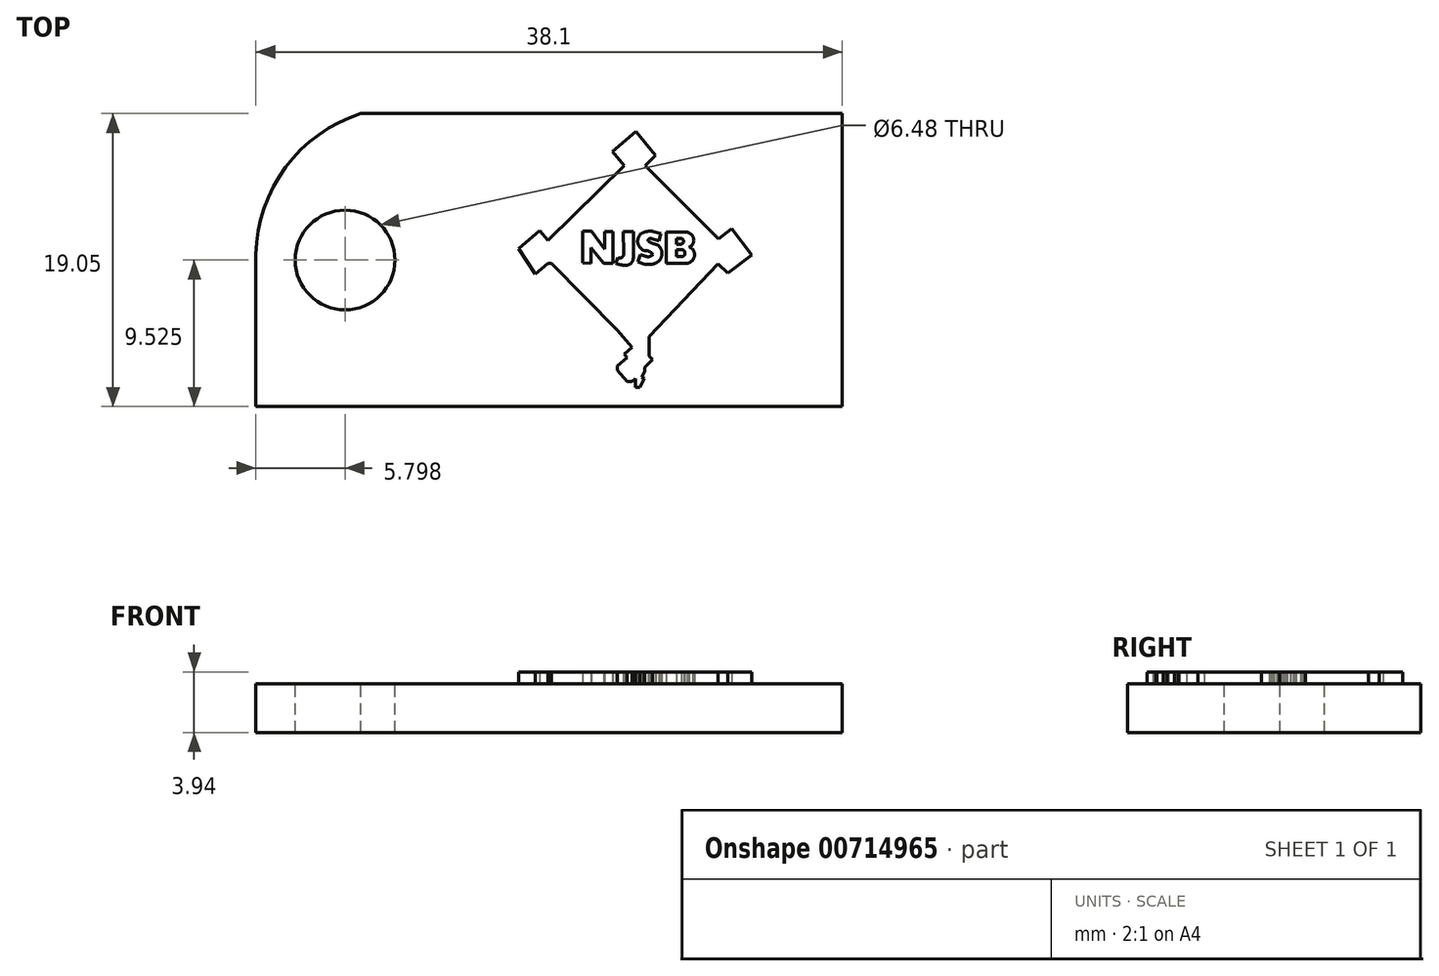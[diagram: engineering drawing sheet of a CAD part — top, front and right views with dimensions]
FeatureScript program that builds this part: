
annotation { "Feature Type Name" : "Feature", "Feature Type Description" : "" }
export const myFeature = defineFeature(function(context is Context, id is Id, definition is map)
    precondition{}
    {
        {
            var Q0;
            Q0=qCreatedBy(makeId("Top.planeOp"),FACE);
            var sketch = newSketch(context, id + "F0", { "sketchPlane" : qUnion([Q0])});
            skLineSegment(sketch, "E0.bottom", {"start": v(0, 0) * mm, "end": v(-38.1, 0) * mm});
            skLineSegment(sketch, "E0.top", {"start": v(0, 19.05) * mm, "end": v(-38.1, 19.05) * mm});
            skLineSegment(sketch, "E0.left", {"start": v(0, 0) * mm, "end": v(0, 19.05) * mm});
            skLineSegment(sketch, "E0.right", {"start": v(-38.1, 0) * mm, "end": v(-38.1, 19.05) * mm});
            skSolve(sketch);
        }
        {
            var Q0;
            Q0=qSketchRegion(id+"F0",true);
            extrude(context, id + "F1", {"entities" : qUnion([Q0]), "depth" : 3.17 * mm, "offsetDistance" : 25.4 * mm});
        }
        {
            var Q0;
            Q0=makeQuery(id+"F1.opExtrude","CAP_FACE",FACE,{"disambiguationData":[OSD([sQuery(id+"F0.wireOp",EDGE,"E0.bottom"),sQuery(id+"F0.wireOp",EDGE,"E0.top"),sQuery(id+"F0.wireOp",EDGE,"E0.left"),sQuery(id+"F0.wireOp",EDGE,"E0.right")])],"isStart":false});
            var sketch = newSketch(context, id + "F2", { "sketchPlane" : qUnion([Q0])});
            skLineSegment(sketch, "E1", {"start": v(-38.1, 9.52) * mm, "end": v(0, 9.52) * mm, "construction": true});
            skArc(sketch, "E2", {"start": v(-31.28, 19.05) * mm, "mid": v(-36.27, 15.42) * mm, "end": v(-38.1, 9.52) * mm});
            skArc(sketch, "E3.MirrorCS", {"start": v(-31.28, 0) * mm, "mid": v(-36.27, 3.63) * mm, "end": v(-38.1, 9.52) * mm});
            skCircle(sketch, "E4", {"center": v(-32.3, 9.52) * mm, "radius": 3.24 * mm});
            skSolve(sketch);
        }
        {
            var Q0;
            {var subQ0=sQuery(id+"F2.wireOp",EDGE,"E2");var subQ1=makeQuery(id+"F1.opExtrude","CAP_EDGE",EDGE,{"disambiguationData":[OSD([sQuery(id+"F0.wireOp",EDGE,"E0.top")])],"isStart":false});var subQ2=makeQuery(id+"F2.imprint","INTERSECT",VERTEX,{"derivedFrom":[subQ1,subQ0]});Q0=makeQuery(id+"F2.imprint","IMPRINT",FACE,{"disambiguationData":[TD([[makeQuery(id+"F2.imprint","IMPRINT",EDGE,{"disambiguationData":[TD([[subQ2,-1.0]])],"derivedFrom":subQ0}),-1.0]])]});}
            var Q1;
            {var subQ0=sQuery(id+"F2.wireOp",EDGE,"E3.MirrorCS");var subQ1=makeQuery(id+"F1.opExtrude","CAP_EDGE",EDGE,{"disambiguationData":[OSD([sQuery(id+"F0.wireOp",EDGE,"E0.bottom")])],"isStart":false});var subQ2=makeQuery(id+"F2.imprint","INTERSECT",VERTEX,{"derivedFrom":[subQ1,subQ0]});Q1=makeQuery(id+"F2.imprint","IMPRINT",FACE,{"disambiguationData":[TD([[makeQuery(id+"F2.imprint","IMPRINT",EDGE,{"disambiguationData":[TD([[subQ2,-1.0]])],"derivedFrom":subQ0}),1.0]])]});}
            var Q2;
            Q2=makeQuery(id+"F2.imprint","IMPRINT",FACE,{"disambiguationData":[TD([[makeQuery(id+"F2.imprint","IMPRINT",EDGE,{"derivedFrom":sQuery(id+"F2.wireOp",EDGE,"E4")}),1.0]])]});
            extrude(context, id + "F3", {"entities" : qUnion([Q0, Q1, Q2]), "operationType" : NewBodyOperationType.REMOVE, "endBound" : BoundingType.THROUGH_ALL, "oppositeDirection" : true, "depth" : 25.4 * mm, "offsetDistance" : 25.4 * mm});
        }
        {
            var Q0;
            Q0=makeQuery(id+"F1.opExtrude","CAP_FACE",FACE,{"disambiguationData":[OSD([sQuery(id+"F0.wireOp",EDGE,"E0.bottom"),sQuery(id+"F0.wireOp",EDGE,"E0.top"),sQuery(id+"F0.wireOp",EDGE,"E0.left"),sQuery(id+"F0.wireOp",EDGE,"E0.right")])],"isStart":false});
            var sketch = newSketch(context, id + "F4", { "sketchPlane" : qUnion([Q0])});
            skLineSegment(sketch, "E5", {"start": v(-13.42, 17.87) * mm, "end": v(-14.93, 16.58) * mm});
            skLineSegment(sketch, "E6", {"start": v(-14.93, 16.58) * mm, "end": v(-14.16, 15.67) * mm});
            skLineSegment(sketch, "E7", {"start": v(-14.16, 15.67) * mm, "end": v(-19.11, 10.8) * mm});
            skLineSegment(sketch, "E8", {"start": v(-19.11, 10.8) * mm, "end": v(-19.65, 11.43) * mm});
            skLineSegment(sketch, "E9", {"start": v(-19.65, 11.43) * mm, "end": v(-21.03, 10.26) * mm});
            skLineSegment(sketch, "E10", {"start": v(-21.03, 10.26) * mm, "end": v(-19.95, 8.6) * mm});
            skLineSegment(sketch, "E11", {"start": v(-19.95, 8.6) * mm, "end": v(-19.11, 9.32) * mm});
            skLineSegment(sketch, "E12", {"start": v(-18.89, 9.32) * mm, "end": v(-14.6, 4.97) * mm});
            skLineSegment(sketch, "E13", {"start": v(-14.6, 4.97) * mm, "end": v(-14.42, 4.75) * mm});
            skLineSegment(sketch, "E14", {"start": v(-14.42, 4.75) * mm, "end": v(-14.17, 4.46) * mm});
            skLineSegment(sketch, "E15", {"start": v(-14.17, 4.46) * mm, "end": v(-13.64, 3.84) * mm});
            skLineSegment(sketch, "E16", {"start": v(-13.64, 3.84) * mm, "end": v(-14.17, 3.4) * mm});
            skLineSegment(sketch, "E17", {"start": v(-14.17, 3.4) * mm, "end": v(-13.99, 3.18) * mm});
            skLineSegment(sketch, "E18", {"start": v(-13.99, 3.18) * mm, "end": v(-14.6, 2.65) * mm});
            skLineSegment(sketch, "E19", {"start": v(-14.6, 2.65) * mm, "end": v(-14.6, 2.37) * mm});
            skLineSegment(sketch, "E20", {"start": v(-14.6, 2.37) * mm, "end": v(-14.35, 2.06) * mm});
            skLineSegment(sketch, "E21", {"start": v(-14.35, 2.06) * mm, "end": v(-13.99, 1.64) * mm});
            skLineSegment(sketch, "E22", {"start": v(-13.99, 1.64) * mm, "end": v(-13.64, 1.64) * mm});
            skLineSegment(sketch, "E23", {"start": v(-13.64, 1.64) * mm, "end": v(-13.43, 1.82) * mm});
            skLineSegment(sketch, "E24", {"start": v(-13.43, 1.82) * mm, "end": v(-13.43, 1.24) * mm});
            skLineSegment(sketch, "E25", {"start": v(-13.43, 1.24) * mm, "end": v(-13.16, 1.24) * mm});
            skLineSegment(sketch, "E26", {"start": v(-13.16, 1.24) * mm, "end": v(-12.87, 1.82) * mm});
            skLineSegment(sketch, "E27", {"start": v(-12.87, 1.82) * mm, "end": v(-13.03, 1.9) * mm});
            skLineSegment(sketch, "E28", {"start": v(-13.03, 1.9) * mm, "end": v(-12.83, 2.3) * mm});
            skLineSegment(sketch, "E29", {"start": v(-12.83, 2.3) * mm, "end": v(-12.83, 2.56) * mm});
            skLineSegment(sketch, "E30", {"start": v(-12.83, 2.56) * mm, "end": v(-12.33, 3.04) * mm});
            skLineSegment(sketch, "E31", {"start": v(-12.33, 3.04) * mm, "end": v(-12.55, 3.28) * mm});
            skLineSegment(sketch, "E32", {"start": v(-12.55, 3.28) * mm, "end": v(-12.55, 3.91) * mm});
            skLineSegment(sketch, "E33", {"start": v(-12.55, 3.91) * mm, "end": v(-12.55, 4.56) * mm});
            skLineSegment(sketch, "E34", {"start": v(-12.55, 4.56) * mm, "end": v(-12.94, 4.56) * mm});
            skLineSegment(sketch, "E35", {"start": v(-12.94, 4.56) * mm, "end": v(-12.94, 5.1) * mm});
            skLineSegment(sketch, "E36", {"start": v(-12.94, 5.1) * mm, "end": v(-12.68, 5.36) * mm});
            skLineSegment(sketch, "E37", {"start": v(-12.68, 5.36) * mm, "end": v(-12.68, 6.07) * mm});
            skLineSegment(sketch, "E38", {"start": v(-12.68, 6.07) * mm, "end": v(-14.16, 6.48) * mm});
            skLineSegment(sketch, "E39", {"start": v(-14.16, 6.48) * mm, "end": v(-14.24, 6.2) * mm});
            skLineSegment(sketch, "E40", {"start": v(-14.24, 6.2) * mm, "end": v(-14.51, 5.62) * mm});
            skLineSegment(sketch, "E41", {"start": v(-14.51, 5.62) * mm, "end": v(-14.51, 5.36) * mm});
            skLineSegment(sketch, "E42", {"start": v(-12.55, 4.56) * mm, "end": v(-8.08, 9.28) * mm});
            skLineSegment(sketch, "E43", {"start": v(-8.08, 9.28) * mm, "end": v(-7.44, 8.67) * mm});
            skLineSegment(sketch, "E44", {"start": v(-7.44, 8.67) * mm, "end": v(-5.9, 9.86) * mm});
            skLineSegment(sketch, "E45", {"start": v(-5.9, 9.86) * mm, "end": v(-7.2, 11.55) * mm});
            skLineSegment(sketch, "E46", {"start": v(-7.2, 11.55) * mm, "end": v(-8.05, 10.9) * mm});
            skLineSegment(sketch, "E47", {"start": v(-8.05, 10.9) * mm, "end": v(-12.8, 15.65) * mm});
            skLineSegment(sketch, "E48", {"start": v(-12.8, 15.65) * mm, "end": v(-12.13, 16.32) * mm});
            skLineSegment(sketch, "E49", {"start": v(-12.13, 16.32) * mm, "end": v(-13.42, 17.87) * mm});
            skLineSegment(sketch, "E50", {"start": v(-16.86, 9.35) * mm, "end": v(-16.86, 11.4) * mm});
            skLineSegment(sketch, "E51", {"start": v(-16.86, 11.4) * mm, "end": v(-16.28, 11.4) * mm});
            skLineSegment(sketch, "E52", {"start": v(-16.28, 11.4) * mm, "end": v(-15.45, 10.21) * mm});
            skLineSegment(sketch, "E53", {"start": v(-15.45, 10.21) * mm, "end": v(-15.45, 11.37) * mm});
            skLineSegment(sketch, "E54", {"start": v(-15.45, 11.37) * mm, "end": v(-14.9, 11.37) * mm});
            skLineSegment(sketch, "E55", {"start": v(-14.9, 11.37) * mm, "end": v(-14.9, 9.31) * mm});
            skLineSegment(sketch, "E56", {"start": v(-14.9, 9.31) * mm, "end": v(-15.5, 9.31) * mm});
            skLineSegment(sketch, "E57", {"start": v(-15.5, 9.31) * mm, "end": v(-16.31, 10.31) * mm});
            skLineSegment(sketch, "E58", {"start": v(-16.31, 10.31) * mm, "end": v(-16.31, 9.31) * mm});
            skLineSegment(sketch, "E59", {"start": v(-16.31, 9.31) * mm, "end": v(-16.86, 9.35) * mm});
            skLineSegment(sketch, "E60", {"start": v(-14.22, 11.37) * mm, "end": v(-13.58, 11.37) * mm});
            skLineSegment(sketch, "E61", {"start": v(-13.58, 11.37) * mm, "end": v(-13.58, 9.64) * mm});
            skArc(sketch, "E62", {"start": v(-14, 9.19) * mm, "mid": v(-13.7, 9.33) * mm, "end": v(-13.58, 9.64) * mm});
            skArc(sketch, "E63", {"start": v(-14.7, 9.3) * mm, "mid": v(-14.36, 9.2) * mm, "end": v(-14, 9.19) * mm});
            skLineSegment(sketch, "E64", {"start": v(-14.7, 9.3) * mm, "end": v(-14.6, 9.7) * mm});
            skArc(sketch, "E65", {"start": v(-14.6, 9.7) * mm, "mid": v(-14.3, 9.7) * mm, "end": v(-14.21, 9.97) * mm});
            skLineSegment(sketch, "E66", {"start": v(-14.21, 9.97) * mm, "end": v(-14.22, 11.37) * mm});
            skLineSegment(sketch, "E67", {"start": v(-11.8, 11.23) * mm, "end": v(-11.92, 10.78) * mm});
            skLineSegment(sketch, "E68", {"start": v(-11.92, 10.78) * mm, "end": v(-12.42, 10.92) * mm});
            skArc(sketch, "E69", {"start": v(-12.42, 10.92) * mm, "mid": v(-12.57, 10.89) * mm, "end": v(-12.62, 10.75) * mm});
            skArc(sketch, "E70", {"start": v(-12.62, 10.75) * mm, "mid": v(-12.37, 10.61) * mm, "end": v(-12.1, 10.55) * mm});
            skArc(sketch, "E71", {"start": v(-11.73, 10.09) * mm, "mid": v(-11.85, 10.37) * mm, "end": v(-12.1, 10.55) * mm});
            skArc(sketch, "E72", {"start": v(-11.84, 9.52) * mm, "mid": v(-11.73, 9.8) * mm, "end": v(-11.73, 10.09) * mm});
            skArc(sketch, "E73", {"start": v(-12.42, 9.25) * mm, "mid": v(-12.1, 9.34) * mm, "end": v(-11.84, 9.52) * mm});
            skLineSegment(sketch, "E74", {"start": v(-12.42, 9.25) * mm, "end": v(-12.83, 9.25) * mm});
            skLineSegment(sketch, "E75", {"start": v(-12.83, 9.25) * mm, "end": v(-13.27, 9.4) * mm});
            skLineSegment(sketch, "E76", {"start": v(-13.27, 9.4) * mm, "end": v(-13.11, 9.88) * mm});
            skLineSegment(sketch, "E77", {"start": v(-13.11, 9.88) * mm, "end": v(-12.73, 9.75) * mm});
            skArc(sketch, "E78", {"start": v(-12.73, 9.75) * mm, "mid": v(-12.5, 9.75) * mm, "end": v(-12.3, 9.88) * mm});
            skArc(sketch, "E79", {"start": v(-12.3, 9.88) * mm, "mid": v(-12.54, 10.09) * mm, "end": v(-12.85, 10.11) * mm});
            skArc(sketch, "E80", {"start": v(-13.28, 10.6) * mm, "mid": v(-13.12, 10.31) * mm, "end": v(-12.85, 10.11) * mm});
            skArc(sketch, "E81", {"start": v(-13.08, 11.23) * mm, "mid": v(-13.26, 10.94) * mm, "end": v(-13.28, 10.6) * mm});
            skArc(sketch, "E82", {"start": v(-12.3, 11.39) * mm, "mid": v(-12.7, 11.38) * mm, "end": v(-13.08, 11.23) * mm});
            skLineSegment(sketch, "E83", {"start": v(-12.3, 11.39) * mm, "end": v(-11.8, 11.23) * mm});
            skLineSegment(sketch, "E84", {"start": v(-11.43, 11.35) * mm, "end": v(-11.43, 9.3) * mm});
            skLineSegment(sketch, "E85", {"start": v(-11.43, 9.3) * mm, "end": v(-10.18, 9.3) * mm});
            skArc(sketch, "E86", {"start": v(-10.18, 9.3) * mm, "mid": v(-9.66, 9.61) * mm, "end": v(-9.71, 10.22) * mm});
            skArc(sketch, "E87", {"start": v(-9.71, 10.22) * mm, "mid": v(-9.82, 10.3) * mm, "end": v(-9.94, 10.36) * mm});
            skArc(sketch, "E88", {"start": v(-9.94, 10.36) * mm, "mid": v(-9.64, 10.82) * mm, "end": v(-9.94, 11.27) * mm});
            skLineSegment(sketch, "E89", {"start": v(-9.94, 11.27) * mm, "end": v(-10.09, 11.33) * mm});
            skLineSegment(sketch, "E90", {"start": v(-10.09, 11.33) * mm, "end": v(-11.43, 11.35) * mm});
            skLineSegment(sketch, "E91", {"start": v(-10.77, 10.2) * mm, "end": v(-10.77, 9.75) * mm});
            skLineSegment(sketch, "E92", {"start": v(-10.77, 9.75) * mm, "end": v(-10.45, 9.75) * mm});
            skArc(sketch, "E93", {"start": v(-10.45, 9.75) * mm, "mid": v(-10.22, 9.97) * mm, "end": v(-10.45, 10.2) * mm});
            skLineSegment(sketch, "E94", {"start": v(-10.45, 10.2) * mm, "end": v(-10.77, 10.2) * mm});
            skLineSegment(sketch, "E95", {"start": v(-10.77, 10.56) * mm, "end": v(-10.5, 10.56) * mm});
            skArc(sketch, "E96", {"start": v(-10.5, 10.56) * mm, "mid": v(-10.3, 10.74) * mm, "end": v(-10.5, 10.93) * mm});
            skLineSegment(sketch, "E97", {"start": v(-10.5, 10.93) * mm, "end": v(-10.77, 10.93) * mm});
            skLineSegment(sketch, "E98", {"start": v(-10.77, 10.93) * mm, "end": v(-10.77, 10.56) * mm});
            skLineSegment(sketch, "E99", {"start": v(-19.11, 9.32) * mm, "end": v(-18.89, 9.32) * mm});
            skLineSegment(sketch, "E100", {"start": v(-14.51, 5.36) * mm, "end": v(-14.6, 4.97) * mm});
            skSolve(sketch);
        }
        {
            var Q0;
            Q0=makeQuery(id+"F4.imprint","IMPRINT",FACE,{"disambiguationData":[TD([[makeQuery(id+"F4.imprint","IMPRINT",EDGE,{"derivedFrom":sQuery(id+"F4.wireOp",EDGE,"E5")}),1.0]])]});
            var Q1;
            Q1=makeQuery(id+"F4.imprint","IMPRINT",FACE,{"disambiguationData":[TD([[makeQuery(id+"F4.imprint","IMPRINT",EDGE,{"derivedFrom":sQuery(id+"F4.wireOp",EDGE,"E91")}),1.0]])]});
            var Q2;
            Q2=makeQuery(id+"F4.imprint","IMPRINT",FACE,{"disambiguationData":[TD([[makeQuery(id+"F4.imprint","IMPRINT",EDGE,{"derivedFrom":sQuery(id+"F4.wireOp",EDGE,"E95")}),1.0]])]});
            var Q3;
            Q3=makeQuery(id+"F4.imprint","IMPRINT",FACE,{"disambiguationData":[TD([[makeQuery(id+"F4.imprint","IMPRINT",EDGE,{"derivedFrom":sQuery(id+"F4.wireOp",EDGE,"E13")}),1.0]])]});
            extrude(context, id + "F5", {"entities" : qUnion([Q0, Q1, Q2, Q3]), "operationType" : NewBodyOperationType.ADD, "depth" : 0.76 * mm, "offsetDistance" : 25.4 * mm});
        }
    });
